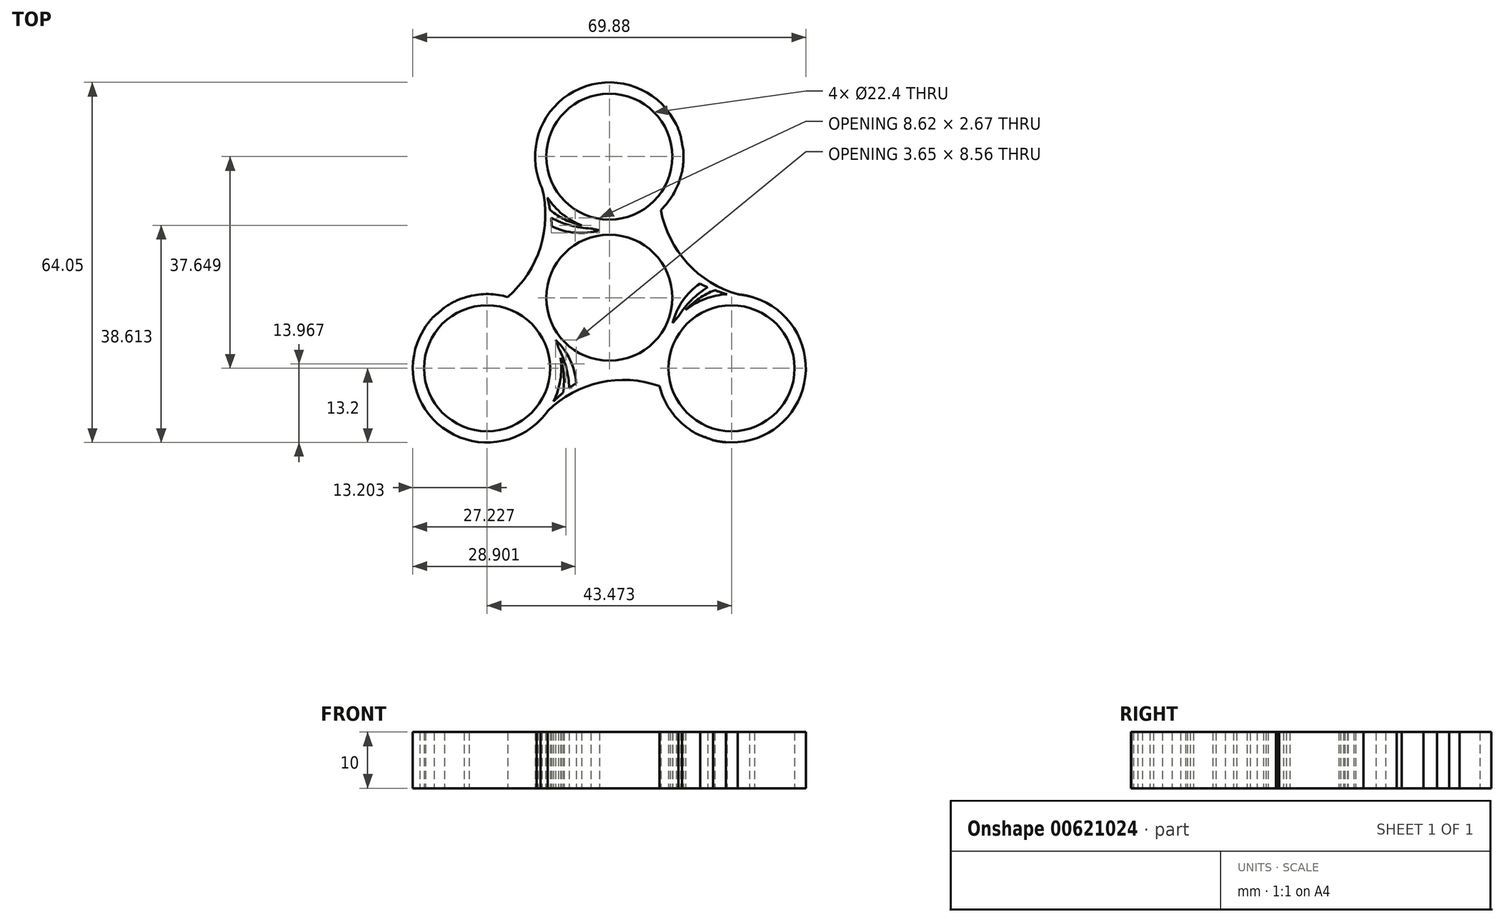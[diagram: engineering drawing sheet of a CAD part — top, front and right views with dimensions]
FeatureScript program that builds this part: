
annotation { "Feature Type Name" : "Feature", "Feature Type Description" : "" }
export const myFeature = defineFeature(function(context is Context, id is Id, definition is map)
    precondition{}
    {
        {
            var Q0;
            Q0=qCreatedBy(makeId("Top.planeOp"),FACE);
            var sketch = newSketch(context, id + "F0", { "sketchPlane" : qUnion([Q0])});
            skCircle(sketch, "E0", {"center": v(0, 0) * mm, "radius": 11.2 * mm});
            skCircle(sketch, "E1", {"center": v(0, 25.1) * mm, "radius": 11.2 * mm});
            skCircle(sketch, "E2", {"center": v(0, 25.1) * mm, "radius": 13.2 * mm});
            skCircle(sketch, "E3.1.0", {"center": v(21.74, -12.55) * mm, "radius": 11.2 * mm});
            skCircle(sketch, "E3.1.1", {"center": v(21.74, -12.55) * mm, "radius": 13.2 * mm});
            skCircle(sketch, "E3.2.0", {"center": v(-21.74, -12.55) * mm, "radius": 11.2 * mm});
            skCircle(sketch, "E3.2.1", {"center": v(-21.74, -12.55) * mm, "radius": 13.2 * mm});
            skLineSegment(sketch, "E3.anchor1", {"start": v(0, 0) * mm, "end": v(0, 25.1) * mm, "construction": true});
            skLineSegment(sketch, "E3.anchor2", {"start": v(0, 0) * mm, "end": v(-21.74, -12.55) * mm, "construction": true});
            skCircle(sketch, "E4.cCircle", {"center": v(0, 0) * mm, "radius": 25.82 * mm, "construction": true});
            skLineSegment(sketch, "E4.0", {"start": v(-0.26, 51.63) * mm, "end": v(44.84, -25.6) * mm});
            skLineSegment(sketch, "E4.1", {"start": v(44.84, -25.6) * mm, "end": v(-44.58, -26.04) * mm});
            skLineSegment(sketch, "E4.2", {"start": v(-44.58, -26.04) * mm, "end": v(-0.26, 51.63) * mm});
            skPoint(sketch, "E4.0.midPoint", {"position": v(22.3, 13.02) * mm});
            skLineSegment(sketch, "E5", {"start": v(0, 25.1) * mm, "end": v(21.74, -12.55) * mm, "construction": true});
            skLineSegment(sketch, "E6", {"start": v(-21.74, -12.55) * mm, "end": v(56.1, 32.4) * mm, "construction": true});
            skArc(sketch, "E7", {"start": v(12.91, 22.35) * mm, "mid": v(14.7, 8.48) * mm, "end": v(25.82, 0) * mm});
            skArc(sketch, "E8.1.0", {"start": v(-25.82, 0) * mm, "mid": v(-14.7, 8.48) * mm, "end": v(-12.91, 22.35) * mm});
            skArc(sketch, "E8.2.0", {"start": v(12.9, -22.36) * mm, "mid": v(0, -16.96) * mm, "end": v(-12.9, -22.36) * mm});
            skArc(sketch, "E9", {"start": v(9.15, 15.59) * mm, "mid": v(13.89, 6.13) * mm, "end": v(22.9, 0.6) * mm});
            skArc(sketch, "E10.1.0", {"start": v(-18.08, 0.13) * mm, "mid": v(-12.25, 8.96) * mm, "end": v(-11.97, 19.53) * mm});
            skArc(sketch, "E10.2.0", {"start": v(8.92, -15.72) * mm, "mid": v(-1.63, -15.1) * mm, "end": v(-10.93, -20.13) * mm});
            skArc(sketch, "E11", {"start": v(5.57, 13.13) * mm, "mid": v(11.93, 5.27) * mm, "end": v(20.92, 0.62) * mm});
            skArc(sketch, "E12.1.0", {"start": v(-14.16, -1.74) * mm, "mid": v(-10.53, 7.7) * mm, "end": v(-11, 17.8) * mm});
            skArc(sketch, "E12.2.0", {"start": v(8.59, -11.4) * mm, "mid": v(-1.4, -12.97) * mm, "end": v(-9.92, -18.43) * mm});
            skArc(sketch, "E13", {"start": v(-10.53, 15.58) * mm, "mid": v(-7.87, 13.89) * mm, "end": v(-4.9, 12.84) * mm});
            skArc(sketch, "E14", {"start": v(-10.35, 14.2) * mm, "mid": v(-6.91, 12.85) * mm, "end": v(-3.26, 12.3) * mm});
            skArc(sketch, "E15", {"start": v(-10.24, 12.71) * mm, "mid": v(-6.05, 11.57) * mm, "end": v(-1.73, 12.01) * mm});
            skArc(sketch, "E16", {"start": v(-10.23, 10.73) * mm, "mid": v(-5.05, 10.74) * mm, "end": v(0, 11.9) * mm});
            skArc(sketch, "E17.1.0", {"start": v(-8.22, -16.91) * mm, "mid": v(-8.09, -13.76) * mm, "end": v(-8.67, -10.66) * mm});
            skArc(sketch, "E17.2.0", {"start": v(18.76, 1.33) * mm, "mid": v(15.96, -0.12) * mm, "end": v(13.57, -2.18) * mm});
            skArc(sketch, "E18.1.0", {"start": v(-7.12, -16.06) * mm, "mid": v(-7.67, -12.41) * mm, "end": v(-9.03, -8.98) * mm});
            skArc(sketch, "E18.2.0", {"start": v(17.47, 1.86) * mm, "mid": v(14.59, -0.44) * mm, "end": v(12.29, -3.33) * mm});
            skArc(sketch, "E19.1.0", {"start": v(-5.89, -15.22) * mm, "mid": v(-7, -11.02) * mm, "end": v(-9.54, -7.5) * mm});
            skArc(sketch, "E19.2.0", {"start": v(16.13, 2.51) * mm, "mid": v(13.04, -0.54) * mm, "end": v(11.27, -4.51) * mm});
            skArc(sketch, "E20.1.0", {"start": v(-4.17, -14.23) * mm, "mid": v(-6.77, -9.74) * mm, "end": v(-10.3, -5.95) * mm});
            skArc(sketch, "E20.2.0", {"start": v(14.4, 3.5) * mm, "mid": v(11.83, -1) * mm, "end": v(10.3, -5.95) * mm});
            skArc(sketch, "E21", {"start": v(12.56, 29.68) * mm, "mid": v(17.95, 12.77) * mm, "end": v(28.72, -1.35) * mm});
            skArc(sketch, "E22.1.0", {"start": v(-31.99, -3.96) * mm, "mid": v(-20.03, 9.17) * mm, "end": v(-13.2, 25.55) * mm});
            skArc(sketch, "E22.2.0", {"start": v(19.43, -25.72) * mm, "mid": v(2.08, -21.93) * mm, "end": v(-15.53, -24.2) * mm});
            skSolve(sketch);
        }
        {
            var Q0;
            {var subQ0=sQuery(id+"F0.wireOp",EDGE,"E13");Q0=makeQuery(id+"F0.imprint","IMPRINT",FACE,{"disambiguationData":[TD([[makeQuery(id+"F0.imprint","IMPRINT",EDGE,{"derivedFrom":subQ0}),-1.0]])]});}
            var Q1;
            {var subQ0=sQuery(id+"F0.wireOp",EDGE,"E10.1.0");Q1=makeQuery(id+"F0.imprint","IMPRINT",FACE,{"disambiguationData":[TD([[makeQuery(id+"F0.imprint","IMPRINT",EDGE,{"derivedFrom":subQ0}),-1.0]])]});}
            var Q2;
            Q2=makeQuery(id+"F0.imprint","IMPRINT",FACE,{"disambiguationData":[TD([[makeQuery(id+"F0.imprint","IMPRINT",EDGE,{"derivedFrom":sQuery(id+"F0.wireOp",EDGE,"E3.2.0")}),-1.0]])]});
            var Q3;
            {var subQ0=sQuery(id+"F0.wireOp",EDGE,"E15");Q3=makeQuery(id+"F0.imprint","IMPRINT",FACE,{"disambiguationData":[TD([[makeQuery(id+"F0.imprint","IMPRINT",EDGE,{"derivedFrom":subQ0}),-1.0]])]});}
            var Q4;
            {var subQ0=sQuery(id+"F0.wireOp",EDGE,"E9");Q4=makeQuery(id+"F0.imprint","IMPRINT",FACE,{"disambiguationData":[TD([[makeQuery(id+"F0.imprint","IMPRINT",EDGE,{"derivedFrom":subQ0}),-1.0]])]});}
            var Q5;
            Q5=makeQuery(id+"F0.imprint","IMPRINT",FACE,{"disambiguationData":[TD([[makeQuery(id+"F0.imprint","IMPRINT",EDGE,{"derivedFrom":sQuery(id+"F0.wireOp",EDGE,"E0")}),-1.0]])]});
            var Q6;
            {var subQ0=sQuery(id+"F0.wireOp",EDGE,"E10.2.0");Q6=makeQuery(id+"F0.imprint","IMPRINT",FACE,{"disambiguationData":[TD([[makeQuery(id+"F0.imprint","IMPRINT",EDGE,{"derivedFrom":subQ0}),-1.0]])]});}
            var Q7;
            {var subQ0=sQuery(id+"F0.wireOp",EDGE,"E17.1.0");Q7=makeQuery(id+"F0.imprint","IMPRINT",FACE,{"disambiguationData":[TD([[makeQuery(id+"F0.imprint","IMPRINT",EDGE,{"derivedFrom":subQ0}),-1.0]])]});}
            var Q8;
            {var subQ0=sQuery(id+"F0.wireOp",EDGE,"E19.1.0");Q8=makeQuery(id+"F0.imprint","IMPRINT",FACE,{"disambiguationData":[TD([[makeQuery(id+"F0.imprint","IMPRINT",EDGE,{"derivedFrom":subQ0}),-1.0]])]});}
            var Q9;
            {var subQ0=sQuery(id+"F0.wireOp",EDGE,"E17.2.0");Q9=makeQuery(id+"F0.imprint","IMPRINT",FACE,{"disambiguationData":[TD([[makeQuery(id+"F0.imprint","IMPRINT",EDGE,{"derivedFrom":subQ0}),-1.0]])]});}
            var Q10;
            {var subQ0=sQuery(id+"F0.wireOp",EDGE,"E19.2.0");Q10=makeQuery(id+"F0.imprint","IMPRINT",FACE,{"disambiguationData":[TD([[makeQuery(id+"F0.imprint","IMPRINT",EDGE,{"derivedFrom":subQ0}),-1.0]])]});}
            var Q11;
            Q11=makeQuery(id+"F0.imprint","IMPRINT",FACE,{"disambiguationData":[TD([[makeQuery(id+"F0.imprint","IMPRINT",EDGE,{"derivedFrom":sQuery(id+"F0.wireOp",EDGE,"E3.1.0")}),-1.0]])]});
            var Q12;
            Q12=makeQuery(id+"F0.imprint","IMPRINT",FACE,{"disambiguationData":[TD([[makeQuery(id+"F0.imprint","IMPRINT",EDGE,{"derivedFrom":sQuery(id+"F0.wireOp",EDGE,"E1")}),-1.0]])]});
            extrude(context, id + "F1", {"entities" : qUnion([Q0, Q1, Q2, Q3, Q4, Q5, Q6, Q7, Q8, Q9, Q10, Q11, Q12]), "depth" : 10 * mm, "offsetDistance" : 25 * mm});
        }
    });
